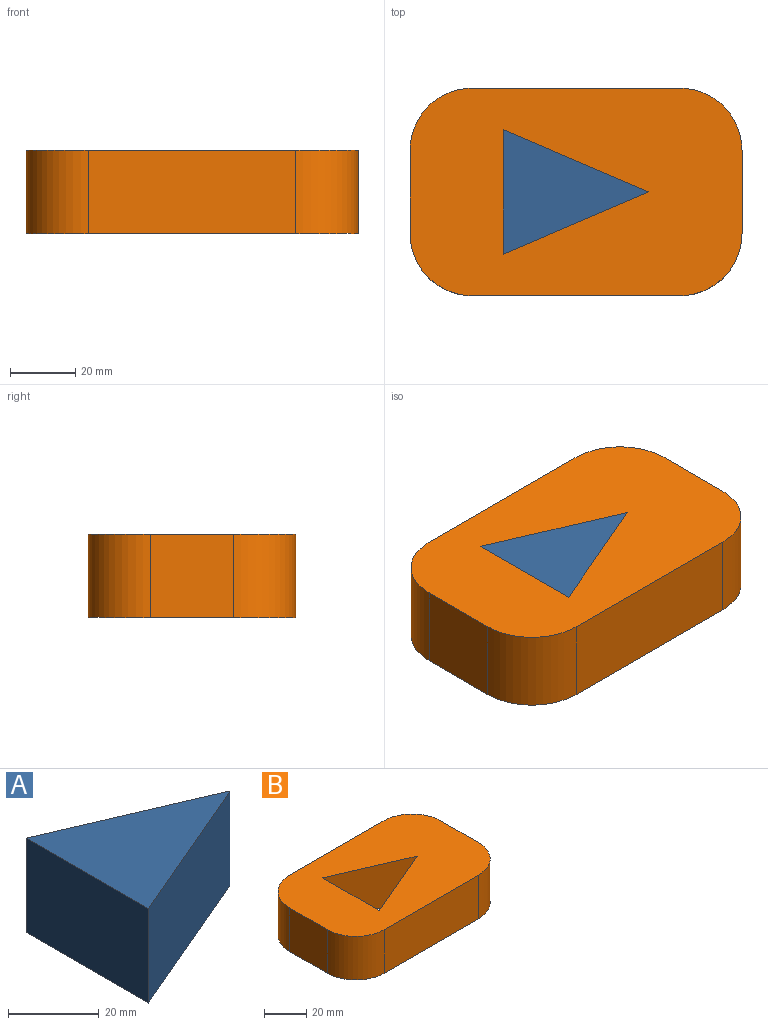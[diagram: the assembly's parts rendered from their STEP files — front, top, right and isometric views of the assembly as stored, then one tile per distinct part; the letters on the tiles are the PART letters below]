
ASSEMBLY  parts=2 mates=1
PART A: 5 faces, bbox 44.5x38.1x25.4 mm
  f0: plane 38.1x25.4mm, normal (-1,0,0), area 967.7mm2, adj f1,f2,f3,f4
  f1: plane 44.45x25.4mm, normal (0.39,-0.92,0), area 1228.3mm2, adj f0,f2,f3,f4
  f2: plane 44.45x25.4mm, normal (0.39,0.92,0), area 1228.3mm2, adj f0,f1,f3,f4
  f3: plane 44.45x38.1mm, normal (0,0,1), area 846.8mm2, adj f0,f1,f2
  f4: plane 44.45x38.1mm, normal (0,0,-1), area 846.8mm2, adj f0,f1,f2
PART B: 13 faces, bbox 101.6x63.5x25.4 mm
  f0: plane 63.5x25.4mm, normal (0,-1,0), area 1612.9mm2, adj f1,f10,f11,f12
  f1: cylinder r=19.05mm len=25.4mm, axis (0,0,-1), area 760.1mm2, adj f0,f2,f11,f12
  f2: plane 25.4x25.4mm, normal (1,0,0), area 645.2mm2, adj f1,f3,f11,f12
  f3: cylinder r=19.05mm len=25.4mm, axis (0,0,-1), area 760.1mm2, adj f2,f4,f11,f12
  f4: plane 63.5x25.4mm, normal (0,1,0), area 1612.9mm2, adj f3,f5,f11,f12
  f5: cylinder r=19.05mm len=25.4mm, axis (0,0,-1), area 760.1mm2, adj f4,f6,f11,f12
  f6: plane 25.4x25.4mm, normal (-1,0,0), area 645.2mm2, adj f5,f10,f11,f12
  f7: plane 44.45x25.4mm, normal (-0.39,0.92,0), area 1228.3mm2, adj f8,f9,f11,f12
  f8: plane 38.1x25.4mm, normal (1,0,0), area 967.7mm2, adj f7,f9,f11,f12
  f9: plane 44.45x25.4mm, normal (-0.39,-0.92,0), area 1228.3mm2, adj f7,f8,f11,f12
  f10: cylinder r=19.05mm len=25.4mm, axis (0,0,-1), area 760.1mm2, adj f0,f6,f11,f12
  f11: plane 101.6x63.5mm, normal (0,0,1), area 5293.3mm2, adj f0,f1,f2,f3,f4,f5,f6,f7
  f12: plane 101.6x63.5mm, normal (0,0,-1), area 5293.3mm2, adj f0,f1,f2,f3,f4,f5,f6,f7
PLACE A at identity
PLACE B at identity
MATE fastened A.f0 <-> B.f8  axis (-1,0,0) through (-22.22,0,12.7)mm
